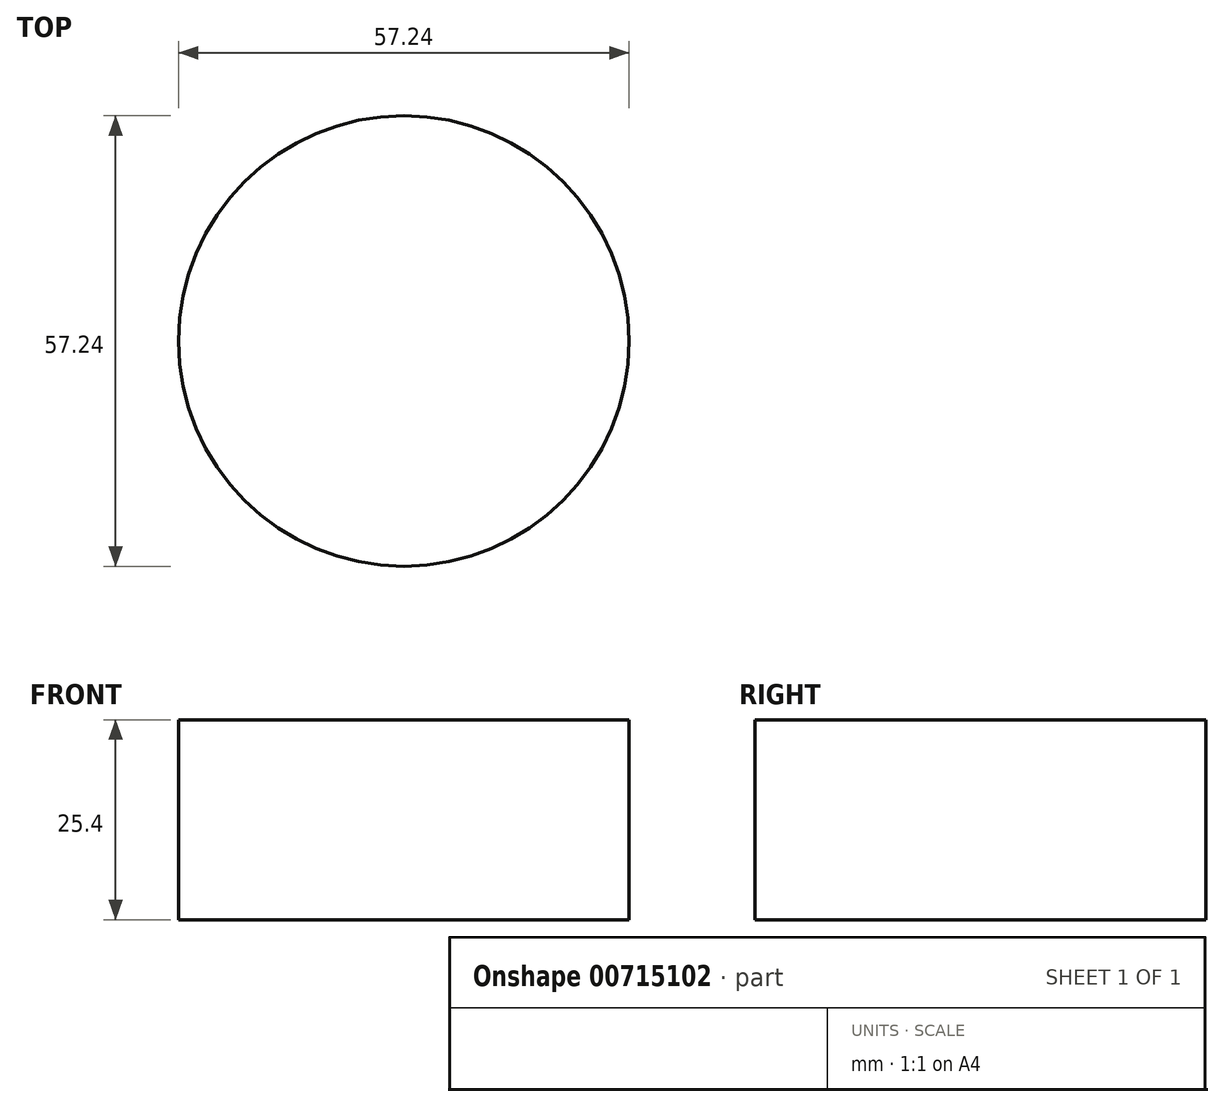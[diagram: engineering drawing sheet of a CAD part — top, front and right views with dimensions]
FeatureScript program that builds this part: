
annotation { "Feature Type Name" : "Feature", "Feature Type Description" : "" }
export const myFeature = defineFeature(function(context is Context, id is Id, definition is map)
    precondition{}
    {
        {
            var Q0;
            Q0=qCreatedBy(makeId("Top.planeOp"),FACE);
            var sketch = newSketch(context, id + "F0", { "sketchPlane" : qUnion([Q0])});
            skCircle(sketch, "E0", {"center": v(0, 0) * mm, "radius": 28.62 * mm});
            skSolve(sketch);
        }
        {
            var Q0;
            Q0 = qSketchRegion(id + "F0", true);
            extrude(context, id + "F1", {"entities" : qUnion([Q0]), "depth" : 25.4 * mm, "offsetDistance" : 25.4 * mm});
        }
    });
